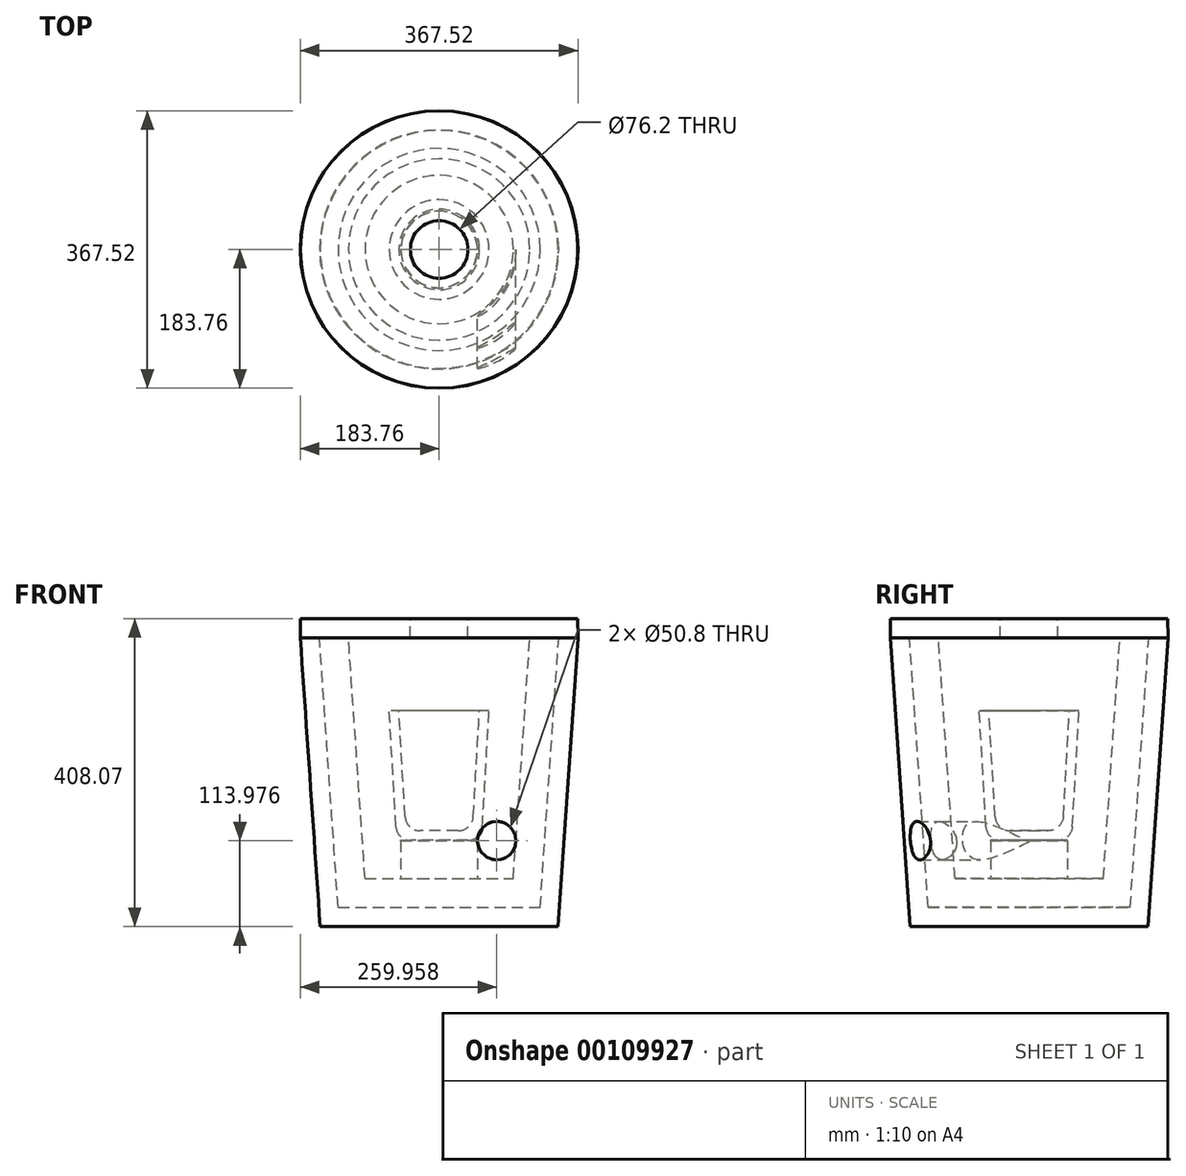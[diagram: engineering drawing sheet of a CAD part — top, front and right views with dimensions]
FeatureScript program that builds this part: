
annotation { "Feature Type Name" : "Feature", "Feature Type Description" : "" }
export const myFeature = defineFeature(function(context is Context, id is Id, definition is map)
    precondition{}
    {
        {
            var Q0;
            Q0=qCreatedBy(makeId("Front.planeOp"),FACE);
            var sketch = newSketch(context, id + "F0", { "sketchPlane" : qUnion([Q0])});
            skLineSegment(sketch, "E0", {"start": v(0, -181.89) * mm, "end": v(157.48, -181.89) * mm});
            skLineSegment(sketch, "E1", {"start": v(157.48, -181.89) * mm, "end": v(183.76, 200.78) * mm});
            skLineSegment(sketch, "E2.0", {"start": v(133.76, -156.49) * mm, "end": v(158.3, 200.78) * mm});
            skLineSegment(sketch, "E2.1", {"start": v(0, -156.49) * mm, "end": v(133.76, -156.49) * mm});
            skLineSegment(sketch, "E3.0", {"start": v(98.2, -118.39) * mm, "end": v(120.11, 200.78) * mm});
            skLineSegment(sketch, "E3.1", {"start": v(0, -118.39) * mm, "end": v(98.2, -118.39) * mm});
            skLineSegment(sketch, "E4", {"start": v(183.76, 200.78) * mm, "end": v(120.11, 200.78) * mm});
            skLineSegment(sketch, "E5.trimOffspring", {"start": v(158.12, 198.18) * mm, "end": v(158.3, 200.78) * mm});
            skLineSegment(sketch, "E6", {"start": v(0, -181.89) * mm, "end": v(0, -118.39) * mm});
            skLineSegment(sketch, "E7", {"start": v(0, 226.18) * mm, "end": v(183.58, 226.18) * mm});
            skLineSegment(sketch, "E8", {"start": v(0, 200.78) * mm, "end": v(183.76, 200.78) * mm});
            skLineSegment(sketch, "E9", {"start": v(0, -118.39) * mm, "end": v(0, 254.3) * mm, "construction": true});
            skPoint(sketch, "E9.endSnap0", {"position": v(0, 214.41) * mm});
            skLineSegment(sketch, "E10", {"start": v(0, -118.39) * mm, "end": v(0, -67.59) * mm});
            skLineSegment(sketch, "E11", {"start": v(0, -67.59) * mm, "end": v(50.8, -67.59) * mm});
            skLineSegment(sketch, "E12", {"start": v(50.8, -67.59) * mm, "end": v(50.8, -118.39) * mm});
            skCircle(sketch, "E13", {"center": v(76.2, -67.91) * mm, "radius": 25.4 * mm});
            skPoint(sketch, "E14.orphan", {"position": v(183.58, 198.22) * mm});
            skLineSegment(sketch, "E15", {"start": v(183.76, 200.78) * mm, "end": v(183.58, 226.18) * mm});
            skLineSegment(sketch, "E16", {"start": v(0, 226.18) * mm, "end": v(0, 200.78) * mm});
            skSolve(sketch);
        }
        {
            var Q0;
            Q0=makeQuery(id+"F0.imprint","IMPRINT",FACE,{"disambiguationData":[TD([[makeQuery(id+"F0.imprint","IMPRINT",EDGE,{"derivedFrom":sQuery(id+"F0.wireOp",EDGE,"E2.0")}),1.0]])]});
            var Q1;
            Q1=sQuery(id+"F0.wireOp",EDGE,"E9");
            revolve(context, id + "F1", {"entities" : qUnion([Q0]), "axis" : qUnion([Q1]), "revolveType" : RevolveType.FULL});
        }
        {
            var Q0;
            {var subQ2=sQuery(id+"F0.wireOp",EDGE,"E0");Q0=makeQuery(id+"F0.imprint","IMPRINT",FACE,{"disambiguationData":[TD([[makeQuery(id+"F0.imprint","IMPRINT",EDGE,{"derivedFrom":subQ2}),1.0]])]});}
            var Q1;
            Q1=sQuery(id+"F0.wireOp",EDGE,"E9");
            revolve(context, id + "F2", {"entities" : qUnion([Q0]), "axis" : qUnion([Q1]), "revolveType" : RevolveType.FULL});
        }
        {
            var Q0;
            {var subQ6=sQuery(id+"F0.wireOp",EDGE,"E10");Q0=makeQuery(id+"F0.imprint","IMPRINT",FACE,{"disambiguationData":[TD([[makeQuery(id+"F0.imprint","IMPRINT",EDGE,{"derivedFrom":subQ6}),-1.0]])]});}
            var Q1;
            Q1=sQuery(id+"F0.wireOp",EDGE,"E9");
            revolve(context, id + "F3", {"entities" : qUnion([Q0]), "axis" : qUnion([Q1]), "revolveType" : RevolveType.FULL});
        }
        {
            var Q0;
            Q0=makeQuery(id+"F0.imprint","IMPRINT",FACE,{"disambiguationData":[TD([[makeQuery(id+"F0.imprint","IMPRINT",EDGE,{"derivedFrom":sQuery(id+"F0.wireOp",EDGE,"E7")}),-1.0]])]});
            var Q1;
            Q1=sQuery(id+"F0.wireOp",EDGE,"E9");
            revolve(context, id + "F4", {"entities" : qUnion([Q0]), "axis" : qUnion([Q1]), "revolveType" : RevolveType.FULL});
        }
        {
            var Q0;
            Q0=sQuery(id+"F0.wireOp",VERTEX,"E13.center");
            var Q1;
            Q1=makeQuery(id+"F2.opRevolve","SWEPT_BODY",BODY,{"disambiguationData":[OSD([sQuery(id+"F0.wireOp",EDGE,"E0"),sQuery(id+"F0.wireOp",EDGE,"E1"),sQuery(id+"F0.wireOp",EDGE,"E2.0"),sQuery(id+"F0.wireOp",EDGE,"E2.1"),sQuery(id+"F0.wireOp",EDGE,"E5.trimOffspring"),sQuery(id+"F0.wireOp",EDGE,"E6"),sQuery(id+"F0.wireOp",EDGE,"E8")])]});
            var Q2;
            Q2=makeQuery(id+"F1.opRevolve","SWEPT_BODY",BODY,{"disambiguationData":[OSD([sQuery(id+"F0.wireOp",EDGE,"E2.0"),sQuery(id+"F0.wireOp",EDGE,"E2.1"),sQuery(id+"F0.wireOp",EDGE,"E3.0"),sQuery(id+"F0.wireOp",EDGE,"E3.1"),sQuery(id+"F0.wireOp",EDGE,"E5.trimOffspring"),sQuery(id+"F0.wireOp",EDGE,"E6"),sQuery(id+"F0.wireOp",EDGE,"E8")])]});
            hole(context, id + "F5", {"style" : HoleStyle.SIMPLE, "endStyle" : HoleEndStyle.THROUGH, "oppositeDirection" : true, "holeDiameter" : 50.8 * mm, "startFromSketch" : true, "locations" : qUnion([Q0]), "scope" : qUnion([Q1, Q2]), "isTappedThrough" : true});
        }
        {
            var Q0;
            Q0=makeQuery(id+"F4.opRevolve","SWEPT_FACE",FACE,{"disambiguationData":[OSD([sQuery(id+"F0.wireOp",EDGE,"E7")])]});
            var sketch = newSketch(context, id + "F6", { "sketchPlane" : qUnion([Q0])});
            skCircle(sketch, "E17", {"center": v(0, 0) * mm, "radius": 44.45 * mm});
            skSolve(sketch);
        }
        {
            var Q0;
            Q0=sQuery(id+"F6.wireOp",VERTEX,"E17.center");
            var Q1;
            Q1=makeQuery(id+"F4.opRevolve","SWEPT_BODY",BODY,{"disambiguationData":[OSD([sQuery(id+"F0.wireOp",EDGE,"WV8v97tG-MOz0-NyO9-0KRc-JftdpRBXcXPT"),sQuery(id+"F0.wireOp",EDGE,"l3r2VzK8-Rc9I-u4uR-QtKG-Q8mmyTudJMLr"),sQuery(id+"F0.wireOp",EDGE,"EoFCriEI-PySf-5ZQT-KHpB-hZyJHHkeXcOO"),sQuery(id+"F0.wireOp",EDGE,"E8")])]});
            hole(context, id + "F7", {"style" : HoleStyle.SIMPLE, "endStyle" : HoleEndStyle.THROUGH, "holeDiameter" : 76.2 * mm, "startFromSketch" : true, "locations" : qUnion([Q0]), "scope" : qUnion([Q1]), "isTappedThrough" : true});
        }
        {
            var Q0;
            Q0=qCreatedBy(makeId("Front.planeOp"),FACE);
            var sketch = newSketch(context, id + "F8", { "sketchPlane" : qUnion([Q0])});
            skLineSegment(sketch, "E18", {"start": v(0, -67.59) * mm, "end": v(38.1, -67.59) * mm});
            skLineSegment(sketch, "E19", {"start": v(57.15, -49.6) * mm, "end": v(66.04, 103.86) * mm});
            skLineSegment(sketch, "E20", {"start": v(66.04, 103.86) * mm, "end": v(53.32, 103.86) * mm});
            skLineSegment(sketch, "E21", {"start": v(0, -54.89) * mm, "end": v(0, -67.59) * mm});
            skArc(sketch, "E22", {"start": v(38.1, -67.59) * mm, "mid": v(51.2, -62.38) * mm, "end": v(57.15, -49.6) * mm});
            skLineSegment(sketch, "E23.0", {"start": v(45.23, -35.85) * mm, "end": v(53.32, 103.86) * mm});
            skLineSegment(sketch, "E23.1", {"start": v(0, -54.89) * mm, "end": v(25.05, -54.89) * mm});
            skArc(sketch, "E24", {"start": v(25.05, -54.89) * mm, "mid": v(38.92, -49.37) * mm, "end": v(45.23, -35.85) * mm});
            skPoint(sketch, "E25.orphan", {"position": v(0, 103.86) * mm});
            skPoint(sketch, "E26.orphan", {"position": v(50.8, 60.38) * mm});
            skSolve(sketch);
        }
        {
            var Q0;
            Q0=makeQuery(id+"F8.imprint","IMPRINT",FACE,{"disambiguationData":[TD([[makeQuery(id+"F8.imprint","IMPRINT",EDGE,{"derivedFrom":sQuery(id+"F8.wireOp",EDGE,"E18")}),1.0]])]});
            var Q1;
            Q1=sQuery(id+"F8.wireOp",EDGE,"E21");
            revolve(context, id + "F9", {"entities" : qUnion([Q0]), "axis" : qUnion([Q1]), "revolveType" : RevolveType.FULL});
        }
    });
